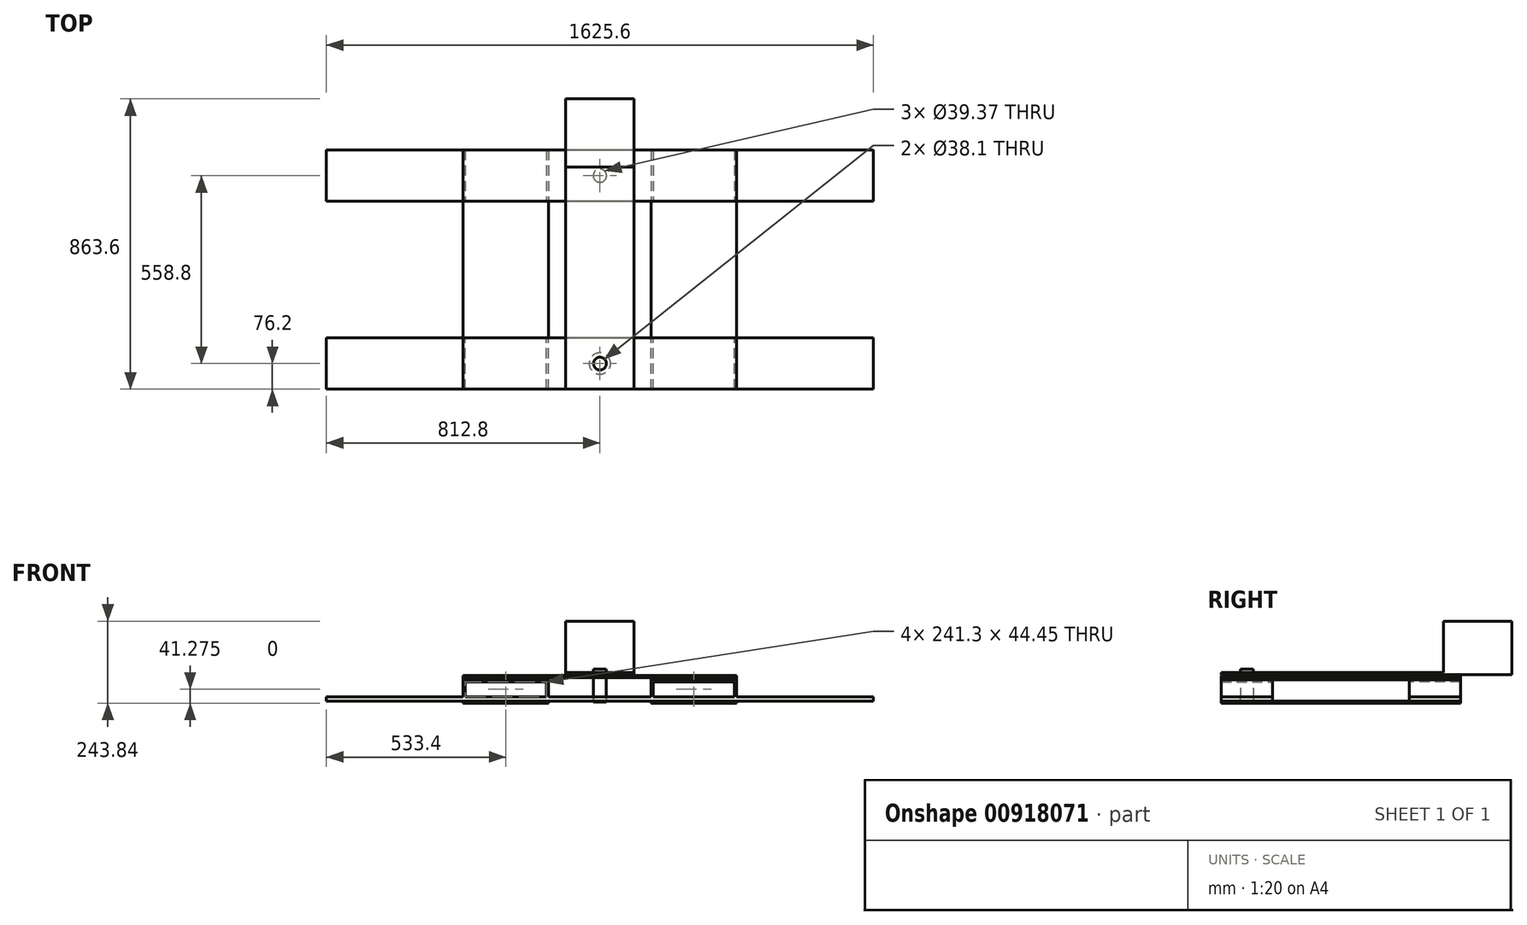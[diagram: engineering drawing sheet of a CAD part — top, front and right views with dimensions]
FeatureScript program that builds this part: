
annotation { "Feature Type Name" : "Feature", "Feature Type Description" : "" }
export const myFeature = defineFeature(function(context is Context, id is Id, definition is map)
    precondition{}
    {
        {
            var Q0;
            Q0=qCreatedBy(makeId("Top.planeOp"),FACE);
            var sketch = newSketch(context, id + "F0", { "sketchPlane" : qUnion([Q0])});
            skLineSegment(sketch, "E0.bottom", {"start": v(-812.8, 203.2) * mm, "end": v(812.8, 203.2) * mm});
            skLineSegment(sketch, "E0.top", {"start": v(-812.8, 355.6) * mm, "end": v(812.8, 355.6) * mm});
            skLineSegment(sketch, "E0.left", {"start": v(-812.8, 203.2) * mm, "end": v(-812.8, 355.6) * mm});
            skLineSegment(sketch, "E0.right", {"start": v(812.8, 203.2) * mm, "end": v(812.8, 355.6) * mm});
            skSolve(sketch);
        }
        {
            var Q0;
            Q0=makeQuery(id+"F0.imprint","IMPRINT",FACE,{"disambiguationData":[TD([[makeQuery(id+"F0.imprint","IMPRINT",EDGE,{"derivedFrom":sQuery(id+"F0.wireOp",EDGE,"E0.bottom")}),1.0]])]});
            extrude(context, id + "F1", {"entities" : qUnion([Q0]), "depth" : 12.7 * mm, "offsetDistance" : 25.4 * mm});
        }
        {
            var Q0;
            Q0=makeQuery(id+"F1.opExtrude","SWEPT_FACE",FACE,{"disambiguationData":[OSD([sQuery(id+"F0.wireOp",EDGE,"E0.bottom")])]});
            var sketch = newSketch(context, id + "F2", { "sketchPlane" : qUnion([Q0])});
            skLineSegment(sketch, "E1", {"start": v(400.05, 12.7) * mm, "end": v(400.05, 57.15) * mm});
            skLineSegment(sketch, "E2", {"start": v(400.05, 57.15) * mm, "end": v(158.75, 57.15) * mm});
            skLineSegment(sketch, "E3", {"start": v(158.75, 57.15) * mm, "end": v(158.75, 12.7) * mm});
            skLineSegment(sketch, "E4", {"start": v(158.75, 12.7) * mm, "end": v(152.4, 12.7) * mm});
            skLineSegment(sketch, "E5", {"start": v(152.4, 12.7) * mm, "end": v(152.4, 63.5) * mm});
            skLineSegment(sketch, "E6", {"start": v(152.4, 63.5) * mm, "end": v(406.4, 63.5) * mm});
            skLineSegment(sketch, "E7", {"start": v(406.4, 63.5) * mm, "end": v(406.4, 12.7) * mm});
            skSolve(sketch);
        }
        {
            var Q0;
            {var subQ0=sQuery(id+"F2.wireOp",EDGE,"E1");Q0=makeQuery(id+"F2.imprint","IMPRINT",FACE,{"disambiguationData":[TD([[makeQuery(id+"F2.imprint","IMPRINT",EDGE,{"derivedFrom":subQ0}),-1.0]])]});}
            var Q1;
            Q1=makeQuery(id+"F1.opExtrude","SWEPT_FACE",FACE,{"disambiguationData":[OSD([sQuery(id+"F0.wireOp",EDGE,"E0.top")])]});
            extrude(context, id + "F3", {"entities" : qUnion([Q0]), "endBound" : BoundingType.UP_TO_SURFACE, "oppositeDirection" : true, "depth" : 25.4 * mm, "endBoundEntityFace" : qUnion([Q1]), "offsetDistance" : 25.4 * mm});
        }
        {
            var Q0;
            Q0=makeQuery(id+"F3.opExtrude","SWEPT_BODY",BODY,{"disambiguationData":[OSD([sQuery(id+"F0.wireOp",EDGE,"E0.bottom"),sQuery(id+"F2.wireOp",EDGE,"E1"),sQuery(id+"F2.wireOp",EDGE,"E2"),sQuery(id+"F2.wireOp",EDGE,"E3"),sQuery(id+"F2.wireOp",EDGE,"E4"),sQuery(id+"F2.wireOp",EDGE,"E5"),sQuery(id+"F2.wireOp",EDGE,"E6"),sQuery(id+"F2.wireOp",EDGE,"E7")])]});
            var Q1;
            Q1=qCreatedBy(makeId("Right.planeOp"),FACE);
            mirror(context, id + "F4", {"operationType" : NewBodyOperationType.ADD, "entities" : qUnion([Q0]), "mirrorPlane" : qUnion([Q1])});
        }
        {
            var Q0;
            Q0=makeQuery(id+"F1.opExtrude","SWEPT_BODY",BODY,{"disambiguationData":[OSD([sQuery(id+"F0.wireOp",EDGE,"E0.bottom"),sQuery(id+"F0.wireOp",EDGE,"E0.top"),sQuery(id+"F0.wireOp",EDGE,"E0.left"),sQuery(id+"F0.wireOp",EDGE,"E0.right")])]});
            var Q1;
            Q1=qCreatedBy(makeId("Front.planeOp"),FACE);
            mirror(context, id + "F5", {"entities" : qUnion([Q0]), "mirrorPlane" : qUnion([Q1])});
        }
        {
            var Q0;
            {var subQ0=makeQuery(id+"F3.opExtrude","CAP_FACE",FACE,{"disambiguationData":[OSD([sQuery(id+"F0.wireOp",EDGE,"E0.bottom"),sQuery(id+"F2.wireOp",EDGE,"E1"),sQuery(id+"F2.wireOp",EDGE,"E2"),sQuery(id+"F2.wireOp",EDGE,"E3"),sQuery(id+"F2.wireOp",EDGE,"E4"),sQuery(id+"F2.wireOp",EDGE,"E5"),sQuery(id+"F2.wireOp",EDGE,"E6"),sQuery(id+"F2.wireOp",EDGE,"E7")])],"isStart":false});Q0=makeQuery(id+"F5.opPattern","COPY",FACE,{"derivedFrom":makeQuery(id+"F4.boolean.opBoolean","MERGE",FACE,{"derivedFrom":[makeQuery(id+"F1.opExtrude","SWEPT_FACE",FACE,{"disambiguationData":[OSD([sQuery(id+"F0.wireOp",EDGE,"E0.top")])]}),subQ0,makeQuery(id+"F4.opPattern","COPY",FACE,{"derivedFrom":subQ0,"instanceName":"1"})]}),"instanceName":"1"});}
            var sketch = newSketch(context, id + "F6", { "sketchPlane" : qUnion([Q0])});
            skLineSegment(sketch, "E8.bottom", {"start": v(-406.4, 63.5) * mm, "end": v(-152.4, 63.5) * mm});
            skLineSegment(sketch, "E8.top", {"start": v(-406.4, 69.85) * mm, "end": v(-152.4, 69.85) * mm});
            skLineSegment(sketch, "E8.left", {"start": v(-406.4, 63.5) * mm, "end": v(-406.4, 69.85) * mm});
            skLineSegment(sketch, "E8.right", {"start": v(-152.4, 63.5) * mm, "end": v(-152.4, 69.85) * mm});
            skPoint(sketch, "E9.oppositeSnap0", {"position": v(-152.4, 66.67) * mm});
            skLineSegment(sketch, "E9.bottom", {"start": v(-406.4, 0) * mm, "end": v(-152.4, 0) * mm});
            skLineSegment(sketch, "E9.top", {"start": v(-406.4, -6.35) * mm, "end": v(-152.4, -6.35) * mm});
            skLineSegment(sketch, "E9.left", {"start": v(-406.4, 0) * mm, "end": v(-406.4, -6.35) * mm});
            skLineSegment(sketch, "E9.right", {"start": v(-152.4, 0) * mm, "end": v(-152.4, -6.35) * mm});
            skSolve(sketch);
        }
        {
            var Q0;
            Q0=makeQuery(id+"F6.imprint","IMPRINT",FACE,{"disambiguationData":[TD([[makeQuery(id+"F6.imprint","IMPRINT",EDGE,{"derivedFrom":sQuery(id+"F6.wireOp",EDGE,"E8.bottom")}),-1.0]])]});
            var Q1;
            Q1=makeQuery(id+"F6.imprint","IMPRINT",FACE,{"disambiguationData":[TD([[makeQuery(id+"F6.imprint","IMPRINT",EDGE,{"derivedFrom":sQuery(id+"F6.wireOp",EDGE,"E9.bottom")}),-1.0]])]});
            var Q2;
            {var subQ0=makeQuery(id+"F3.opExtrude","CAP_FACE",FACE,{"disambiguationData":[OSD([sQuery(id+"F0.wireOp",EDGE,"E0.bottom"),sQuery(id+"F2.wireOp",EDGE,"E1"),sQuery(id+"F2.wireOp",EDGE,"E2"),sQuery(id+"F2.wireOp",EDGE,"E3"),sQuery(id+"F2.wireOp",EDGE,"E4"),sQuery(id+"F2.wireOp",EDGE,"E5"),sQuery(id+"F2.wireOp",EDGE,"E6"),sQuery(id+"F2.wireOp",EDGE,"E7")])],"isStart":false});Q2=makeQuery(id+"F4.boolean.opBoolean","MERGE",FACE,{"derivedFrom":[makeQuery(id+"F1.opExtrude","SWEPT_FACE",FACE,{"disambiguationData":[OSD([sQuery(id+"F0.wireOp",EDGE,"E0.top")])]}),subQ0,makeQuery(id+"F4.opPattern","COPY",FACE,{"derivedFrom":subQ0,"instanceName":"1"})]});}
            extrude(context, id + "F7", {"entities" : qUnion([Q0, Q1]), "endBound" : BoundingType.UP_TO_SURFACE, "oppositeDirection" : true, "depth" : 25.4 * mm, "endBoundEntityFace" : qUnion([Q2]), "offsetDistance" : 25.4 * mm});
        }
        {
            var Q0;
            Q0=makeQuery(id+"F7.opExtrude","SWEPT_BODY",BODY,{"disambiguationData":[OSD([sQuery(id+"F6.wireOp",EDGE,"E8.bottom"),sQuery(id+"F6.wireOp",EDGE,"E8.top"),sQuery(id+"F6.wireOp",EDGE,"E8.left"),sQuery(id+"F6.wireOp",EDGE,"E8.right")])]});
            var Q1;
            Q1=makeQuery(id+"F7.opExtrude","SWEPT_BODY",BODY,{"disambiguationData":[OSD([sQuery(id+"F6.wireOp",EDGE,"E9.bottom"),sQuery(id+"F6.wireOp",EDGE,"E9.top"),sQuery(id+"F6.wireOp",EDGE,"E9.left"),sQuery(id+"F6.wireOp",EDGE,"E9.right")])]});
            var Q2;
            Q2=qCreatedBy(makeId("Right.planeOp"),FACE);
            mirror(context, id + "F8", {"entities" : qUnion([Q0, Q1]), "mirrorPlane" : qUnion([Q2])});
        }
        {
            var Q0;
            Q0=makeQuery(id+"F5.opPattern","COPY",FACE,{"derivedFrom":makeQuery(id+"F4.opPattern","COPY",FACE,{"derivedFrom":makeQuery(id+"F3.opExtrude","SWEPT_FACE",FACE,{"disambiguationData":[OSD([sQuery(id+"F2.wireOp",EDGE,"E7")])]}),"instanceName":"1"}),"instanceName":"1"});
            var sketch = newSketch(context, id + "F9", { "sketchPlane" : qUnion([Q0])});
            skLineSegment(sketch, "E10.bottom", {"start": v(203.2, 76.2) * mm, "end": v(355.6, 76.2) * mm});
            skLineSegment(sketch, "E10.top", {"start": v(203.2, 69.85) * mm, "end": v(355.6, 69.85) * mm});
            skLineSegment(sketch, "E10.left", {"start": v(203.2, 76.2) * mm, "end": v(203.2, 69.85) * mm});
            skLineSegment(sketch, "E10.right", {"start": v(355.6, 76.2) * mm, "end": v(355.6, 69.85) * mm});
            skSolve(sketch);
        }
        {
            var Q0;
            Q0=makeQuery(id+"F9.imprint","IMPRINT",FACE,{"disambiguationData":[TD([[makeQuery(id+"F9.imprint","IMPRINT",EDGE,{"derivedFrom":sQuery(id+"F9.wireOp",EDGE,"E10.bottom")}),-1.0]])]});
            var Q1;
            Q1=makeQuery(id+"F5.opPattern","COPY",FACE,{"derivedFrom":makeQuery(id+"F3.opExtrude","SWEPT_FACE",FACE,{"disambiguationData":[OSD([sQuery(id+"F2.wireOp",EDGE,"E7")])]}),"instanceName":"1"});
            extrude(context, id + "F10", {"entities" : qUnion([Q0]), "endBound" : BoundingType.UP_TO_SURFACE, "oppositeDirection" : true, "depth" : 25.4 * mm, "endBoundEntityFace" : qUnion([Q1]), "offsetDistance" : 25.4 * mm});
        }
        {
            var Q0;
            Q0=makeQuery(id+"F10.opExtrude","SWEPT_FACE",FACE,{"disambiguationData":[OSD([sQuery(id+"F9.wireOp",EDGE,"E10.bottom")])]});
            var sketch = newSketch(context, id + "F11", { "sketchPlane" : qUnion([Q0])});
            skPoint(sketch, "E11", {"position": v(0, -279.4) * mm});
            skCircle(sketch, "E12", {"center": v(0, -279.4) * mm, "radius": 19.05 * mm});
            skCircle(sketch, "E13", {"center": v(0, -279.4) * mm, "radius": 31.75 * mm});
            skSolve(sketch);
        }
        {
            var Q0;
            Q0=sQuery(id+"F11.wireOp",VERTEX,"E11");
            var Q1;
            Q1=makeQuery(id+"F5.opPattern","COPY",BODY,{"derivedFrom":makeQuery(id+"F1.opExtrude","SWEPT_BODY",BODY,{"disambiguationData":[OSD([sQuery(id+"F0.wireOp",EDGE,"E0.bottom"),sQuery(id+"F0.wireOp",EDGE,"E0.top"),sQuery(id+"F0.wireOp",EDGE,"E0.left"),sQuery(id+"F0.wireOp",EDGE,"E0.right")])]}),"instanceName":"1"});
            var Q2;
            Q2=makeQuery(id+"F10.opExtrude","SWEPT_BODY",BODY,{"disambiguationData":[OSD([sQuery(id+"F9.wireOp",EDGE,"E10.bottom"),sQuery(id+"F9.wireOp",EDGE,"E10.top"),sQuery(id+"F9.wireOp",EDGE,"E10.left"),sQuery(id+"F9.wireOp",EDGE,"E10.right")])]});
            hole(context, id + "F12", {"style" : HoleStyle.SIMPLE, "endStyle" : HoleEndStyle.THROUGH, "holeDiameter" : 39.37 * mm, "majorDiameter" : 6.35 * mm, "isTappedThrough" : true, "tappedDepth" : 12.7 * mm, "tapClearance" : 3, "startFromSketch" : true, "locations" : qUnion([Q0]), "scope" : qUnion([Q1, Q2])});
        }
        {
            var Q0;
            Q0=makeQuery(id+"F11.imprint","IMPRINT",FACE,{"disambiguationData":[TD([[makeQuery(id+"F11.imprint","IMPRINT",EDGE,{"derivedFrom":sQuery(id+"F11.wireOp",EDGE,"E12")}),1.0]])]});
            extrude(context, id + "F13", {"entities" : qUnion([Q0]), "depth" : 19.05 * mm, "offsetDistance" : 25.4 * mm});
        }
        {
            var Q0;
            Q0=makeQuery(id+"F11.imprint","IMPRINT",FACE,{"disambiguationData":[TD([[makeQuery(id+"F11.imprint","IMPRINT",EDGE,{"derivedFrom":sQuery(id+"F11.wireOp",EDGE,"E12")}),1.0]])]});
            var Q1;
            Q1=sQuery(id+"F11.wireOp",EDGE,"E12");
            extrude(context, id + "F14", {"entities" : qUnion([Q0]), "operationType" : NewBodyOperationType.ADD, "surfaceEntities" : qUnion([Q1]), "oppositeDirection" : true, "depth" : 78.74 * mm, "offsetDistance" : 25.4 * mm});
        }
        {
            var Q0;
            Q0=makeQuery(id+"F11.imprint","IMPRINT",FACE,{"disambiguationData":[TD([[makeQuery(id+"F11.imprint","IMPRINT",EDGE,{"derivedFrom":sQuery(id+"F11.wireOp",EDGE,"E12")}),-1.0]])]});
            extrude(context, id + "F15", {"entities" : qUnion([Q0]), "depth" : 2.54 * mm, "offsetDistance" : 25.4 * mm});
        }
        {
            var Q0;
            Q0=makeQuery(id+"F15.opExtrude","CAP_FACE",FACE,{"disambiguationData":[OSD([sQuery(id+"F11.wireOp",EDGE,"E12"),sQuery(id+"F11.wireOp",EDGE,"E13")])],"isStart":false});
            var sketch = newSketch(context, id + "F16", { "sketchPlane" : qUnion([Q0])});
            skLineSegment(sketch, "E14.bottom", {"start": v(101.6, -355.6) * mm, "end": v(-101.6, -355.6) * mm});
            skLineSegment(sketch, "E14.top", {"start": v(101.6, 508) * mm, "end": v(-101.6, 508) * mm});
            skLineSegment(sketch, "E14.left", {"start": v(101.6, -355.6) * mm, "end": v(101.6, 508) * mm});
            skLineSegment(sketch, "E14.right", {"start": v(-101.6, -355.6) * mm, "end": v(-101.6, 508) * mm});
            skSolve(sketch);
        }
        {
            var Q0;
            Q0=makeQuery(id+"F16.imprint","IMPRINT",FACE,{"disambiguationData":[TD([[makeQuery(id+"F16.imprint","IMPRINT",EDGE,{"derivedFrom":sQuery(id+"F16.wireOp",EDGE,"E14.bottom")}),-1.0]])]});
            var Q1;
            Q1=makeQuery(id+"F16.imprint","IMPRINT",FACE,{"disambiguationData":[TD([[makeQuery(id+"F16.imprint","IMPRINT",EDGE,{"derivedFrom":makeQuery(id+"F15.opExtrude","CAP_EDGE",EDGE,{"disambiguationData":[OSD([sQuery(id+"F11.wireOp",EDGE,"E12")])],"isStart":false})}),-1.0]])]});
            extrude(context, id + "F17", {"entities" : qUnion([Q0, Q1]), "depth" : 6.35 * mm, "offsetDistance" : 25.4 * mm});
        }
        {
            var Q0;
            Q0=makeQuery(id+"F17.opExtrude","CAP_FACE",FACE,{"disambiguationData":[OSD([sQuery(id+"F11.wireOp",EDGE,"E12"),sQuery(id+"F16.wireOp",EDGE,"E14.bottom"),sQuery(id+"F16.wireOp",EDGE,"E14.top"),sQuery(id+"F16.wireOp",EDGE,"E14.left"),sQuery(id+"F16.wireOp",EDGE,"E14.right")])],"isStart":false});
            var sketch = newSketch(context, id + "F18", { "sketchPlane" : qUnion([Q0])});
            skLineSegment(sketch, "E15.bottom", {"start": v(-101.6, 508) * mm, "end": v(101.6, 508) * mm});
            skLineSegment(sketch, "E15.top", {"start": v(-101.6, 304.8) * mm, "end": v(101.6, 304.8) * mm});
            skLineSegment(sketch, "E15.left", {"start": v(-101.6, 508) * mm, "end": v(-101.6, 304.8) * mm});
            skLineSegment(sketch, "E15.right", {"start": v(101.6, 508) * mm, "end": v(101.6, 304.8) * mm});
            skSolve(sketch);
        }
        {
            var Q0;
            Q0=makeQuery(id+"F18.imprint","IMPRINT",FACE,{"disambiguationData":[TD([[makeQuery(id+"F18.imprint","IMPRINT",EDGE,{"derivedFrom":sQuery(id+"F18.wireOp",EDGE,"E15.bottom")}),1.0]])]});
            extrude(context, id + "F19", {"entities" : qUnion([Q0]), "operationType" : NewBodyOperationType.ADD, "depth" : 152.4 * mm, "offsetDistance" : 25.4 * mm});
        }
        {
            var Q0;
            Q0=makeQuery(id+"F10.opExtrude","SWEPT_BODY",BODY,{"disambiguationData":[OSD([sQuery(id+"F9.wireOp",EDGE,"E10.bottom"),sQuery(id+"F9.wireOp",EDGE,"E10.top"),sQuery(id+"F9.wireOp",EDGE,"E10.left"),sQuery(id+"F9.wireOp",EDGE,"E10.right")])]});
            var Q1;
            Q1=qCreatedBy(makeId("Front.planeOp"),FACE);
            mirror(context, id + "F20", {"entities" : qUnion([Q0]), "mirrorPlane" : qUnion([Q1])});
        }
    });
